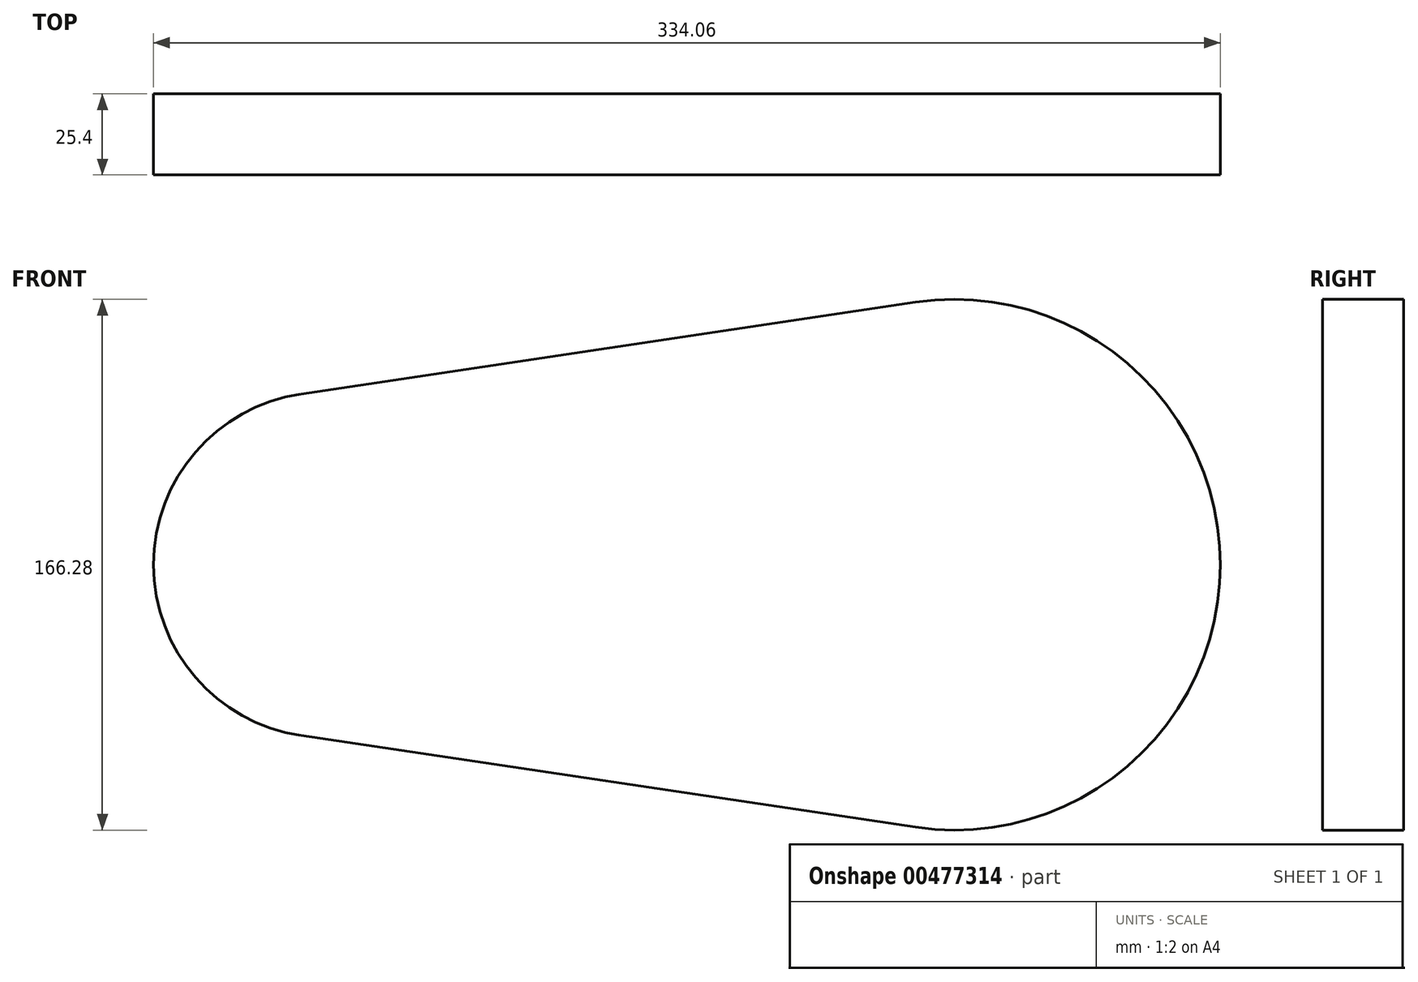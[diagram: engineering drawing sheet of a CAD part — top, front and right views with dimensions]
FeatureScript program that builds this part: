
annotation { "Feature Type Name" : "Feature", "Feature Type Description" : "" }
export const myFeature = defineFeature(function(context is Context, id is Id, definition is map)
    precondition{}
    {
        {
            var Q0;
            Q0=qCreatedBy(makeId("Front.planeOp"),FACE);
            var sketch = newSketch(context, id + "F0", { "sketchPlane" : qUnion([Q0])});
            skArc(sketch, "E0", {"start": v(-115.85, 53.52) * mm, "mid": v(-161.98, 0) * mm, "end": v(-115.85, -53.52) * mm});
            skArc(sketch, "E1", {"start": v(76.67, -82.23) * mm, "mid": v(172.08, 0) * mm, "end": v(76.67, 82.23) * mm});
            skLineSegment(sketch, "E2", {"start": v(-115.85, 53.52) * mm, "end": v(76.67, 82.23) * mm});
            skLineSegment(sketch, "E3", {"start": v(76.67, -82.23) * mm, "end": v(-115.85, -53.52) * mm});
            skSolve(sketch);
        }
        {
            var Q0;
            Q0=makeQuery(id+"F0.imprint","IMPRINT",FACE,{"disambiguationData":[TD([[makeQuery(id+"F0.imprint","IMPRINT",EDGE,{"derivedFrom":sQuery(id+"F0.wireOp",EDGE,"E0")}),1.0]])]});
            extrude(context, id + "F1", {"entities" : qUnion([Q0]), "depth" : 25.4 * mm});
        }
    });
